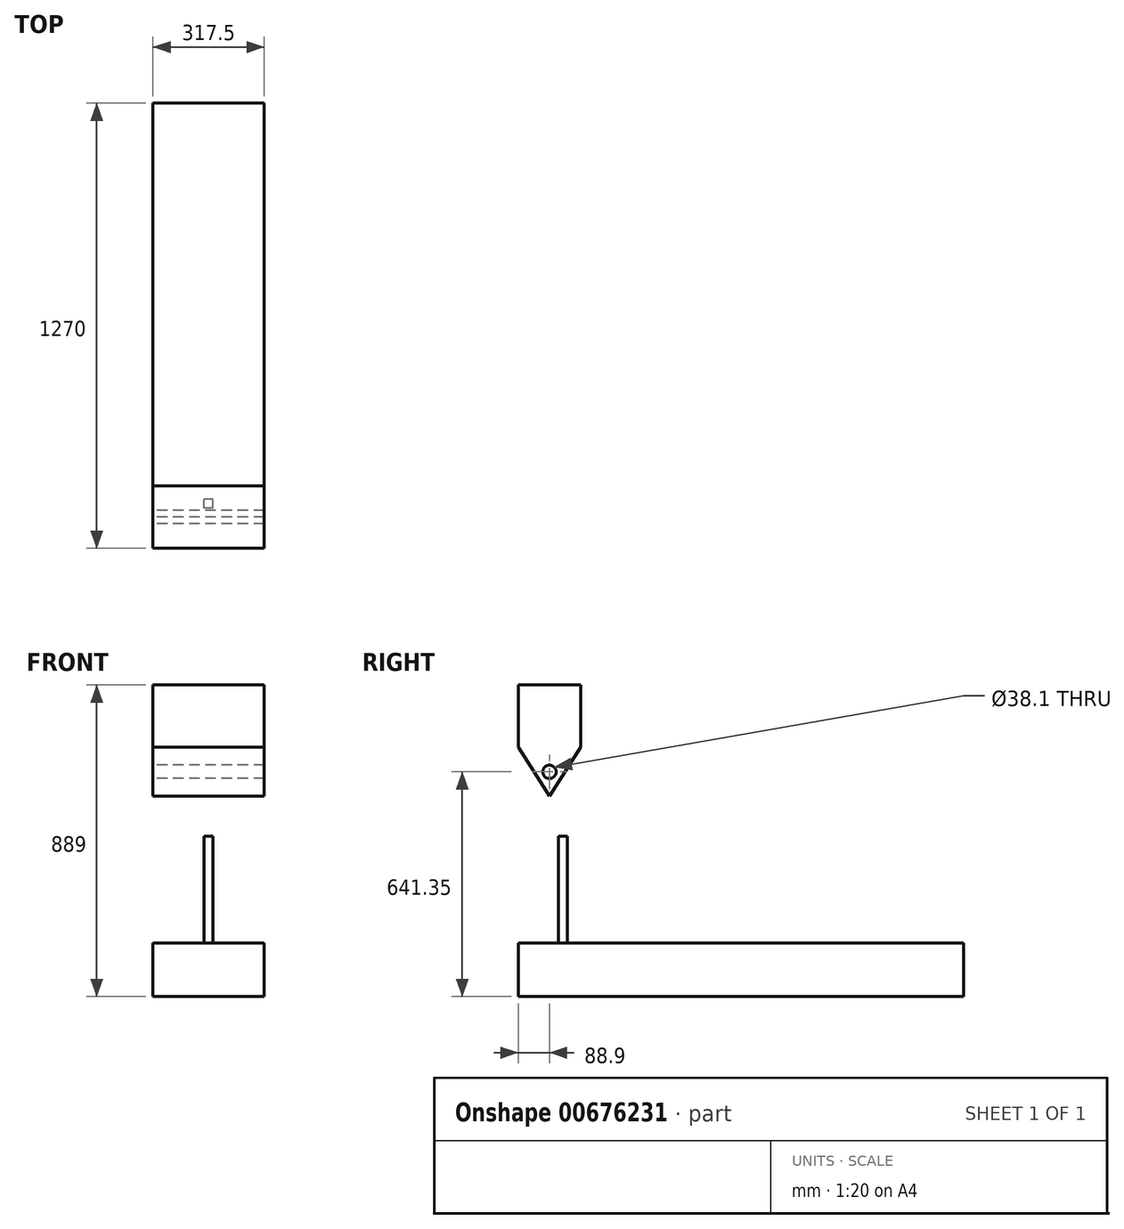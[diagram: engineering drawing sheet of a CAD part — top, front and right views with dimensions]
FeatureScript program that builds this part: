
annotation { "Feature Type Name" : "Feature", "Feature Type Description" : "" }
export const myFeature = defineFeature(function(context is Context, id is Id, definition is map)
    precondition{}
    {
        {
            var Q0;
            Q0=qCreatedBy(makeId("Right.planeOp"),FACE);
            var sketch = newSketch(context, id + "F0", { "sketchPlane" : qUnion([Q0])});
            skLineSegment(sketch, "E0.bottom", {"start": v(0, 0) * mm, "end": v(1270, 0) * mm});
            skLineSegment(sketch, "E0.top", {"start": v(0, -152.4) * mm, "end": v(1270, -152.4) * mm});
            skLineSegment(sketch, "E0.left", {"start": v(0, 0) * mm, "end": v(0, -152.4) * mm});
            skLineSegment(sketch, "E0.right", {"start": v(1270, 0) * mm, "end": v(1270, -152.4) * mm});
            skLineSegment(sketch, "E1.bottom", {"start": v(0, 736.6) * mm, "end": v(177.8, 736.6) * mm});
            skLineSegment(sketch, "E1.top", {"start": v(0, 558.8) * mm, "end": v(177.8, 558.8) * mm});
            skLineSegment(sketch, "E1.left", {"start": v(0, 736.6) * mm, "end": v(0, 558.8) * mm});
            skLineSegment(sketch, "E1.right", {"start": v(177.8, 736.6) * mm, "end": v(177.8, 558.8) * mm});
            skLineSegment(sketch, "E2", {"start": v(0, 558.8) * mm, "end": v(88.9, 419.1) * mm});
            skLineSegment(sketch, "E3", {"start": v(88.9, 419.1) * mm, "end": v(177.8, 558.8) * mm});
            skCircle(sketch, "E4", {"center": v(88.9, 488.95) * mm, "radius": 19.05 * mm});
            skLineSegment(sketch, "E5", {"start": v(88.9, 558.8) * mm, "end": v(88.9, 419.1) * mm, "construction": true});
            skLineSegment(sketch, "E6", {"start": v(114.3, 0) * mm, "end": v(114.3, 304.8) * mm});
            skLineSegment(sketch, "E7", {"start": v(114.3, 304.8) * mm, "end": v(139.7, 304.8) * mm});
            skLineSegment(sketch, "E8", {"start": v(139.7, 304.8) * mm, "end": v(139.7, 0) * mm});
            skSolve(sketch);
        }
        {
            var Q0;
            Q0=makeQuery(id+"F0.imprint","IMPRINT",FACE,{"disambiguationData":[TD([[makeQuery(id+"F0.imprint","IMPRINT",EDGE,{"derivedFrom":sQuery(id+"F0.wireOp",EDGE,"E1.bottom")}),-1.0]])]});
            var Q1;
            Q1=makeQuery(id+"F0.imprint","IMPRINT",FACE,{"disambiguationData":[TD([[makeQuery(id+"F0.imprint","IMPRINT",EDGE,{"derivedFrom":sQuery(id+"F0.wireOp",EDGE,"E1.top")}),-1.0]])]});
            var Q2;
            Q2=makeQuery(id+"F0.imprint","IMPRINT",FACE,{"disambiguationData":[TD([[makeQuery(id+"F0.imprint","IMPRINT",EDGE,{"derivedFrom":sQuery(id+"F0.wireOp",EDGE,"E0.top")}),1.0]])]});
            extrude(context, id + "F1", {"entities" : qUnion([Q0, Q1, Q2]), "flatOperationType" : FlatOperationType.REMOVE, "depth" : 158.75 * mm, "offsetDistance" : 25.4 * mm, "hasSecondDirection" : true, "secondDirectionOppositeDirection" : true, "secondDirectionDepth" : 158.75 * mm, "domain" : OperationDomain.MODEL});
        }
        {
            var Q0;
            {var subQ0=sQuery(id+"F0.wireOp",EDGE,"E6");Q0=makeQuery(id+"F0.imprint","IMPRINT",FACE,{"disambiguationData":[TD([[makeQuery(id+"F0.imprint","IMPRINT",EDGE,{"derivedFrom":subQ0}),-1.0]])]});}
            extrude(context, id + "F2", {"entities" : qUnion([Q0]), "operationType" : NewBodyOperationType.ADD, "depth" : 12.7 * mm, "offsetDistance" : 25.4 * mm, "hasSecondDirection" : true, "secondDirectionOppositeDirection" : true, "secondDirectionDepth" : 12.7 * mm});
        }
    });
